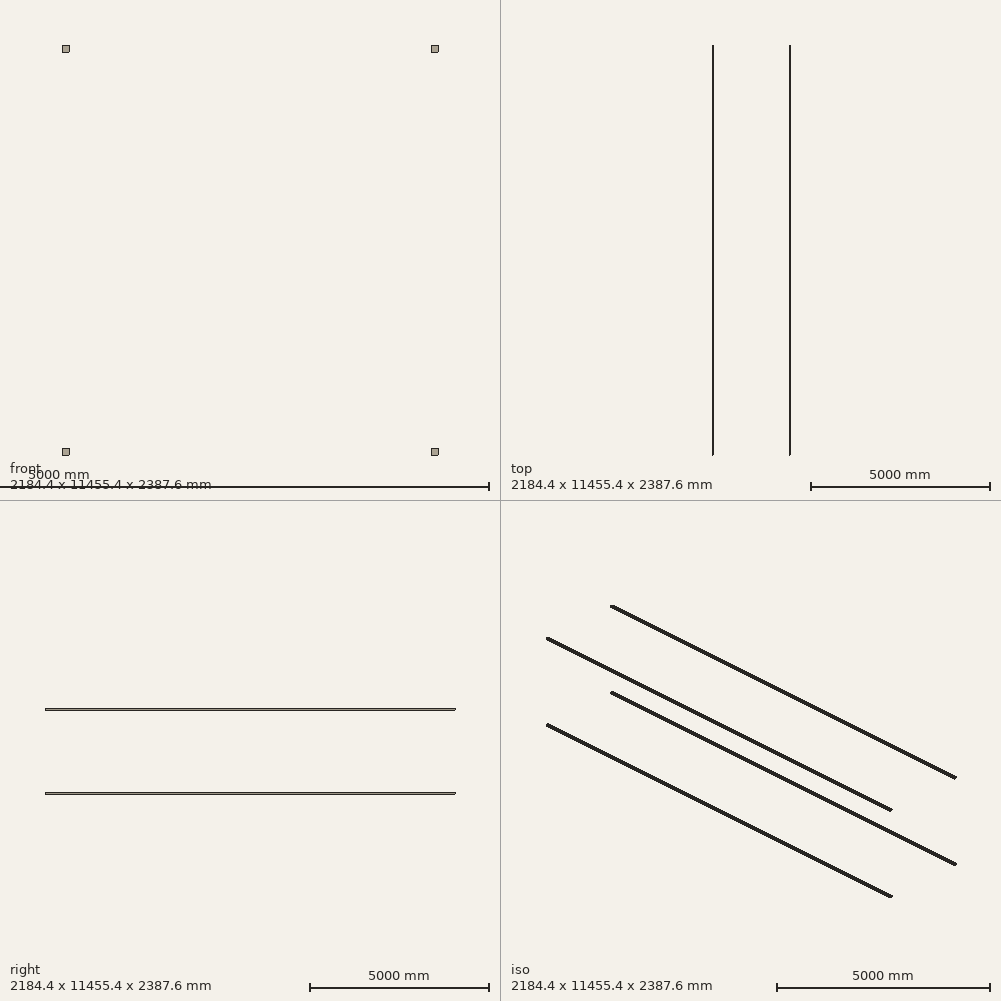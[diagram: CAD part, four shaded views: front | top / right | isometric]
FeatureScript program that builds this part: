
annotation { "Feature Type Name" : "Feature", "Feature Type Description" : "" }
export const myFeature = defineFeature(function(context is Context, id is Id, definition is map)
    precondition{}
    {
        {
            var Q0;
            Q0=qCreatedBy(makeId("Front.planeOp"),FACE);
            var sketch = newSketch(context, id + "F0", { "sketchPlane" : qUnion([Q0])});
            skLineSegment(sketch, "E0.bottom", {"start": v(-263.25, -179.2) * mm, "end": v(-225.15, -179.2) * mm});
            skLineSegment(sketch, "E0.top", {"start": v(-263.25, -217.3) * mm, "end": v(-225.15, -217.3) * mm});
            skLineSegment(sketch, "E0.left", {"start": v(-263.25, -179.2) * mm, "end": v(-263.25, -217.3) * mm});
            skLineSegment(sketch, "E0.right", {"start": v(-225.15, -179.2) * mm, "end": v(-225.15, -217.3) * mm});
            skLineSegment(sketch, "E1.bottom", {"start": v(1883.05, -179.2) * mm, "end": v(1921.15, -179.2) * mm});
            skLineSegment(sketch, "E1.top", {"start": v(1883.05, -217.3) * mm, "end": v(1921.15, -217.3) * mm});
            skLineSegment(sketch, "E1.left", {"start": v(1883.05, -179.2) * mm, "end": v(1883.05, -217.3) * mm});
            skLineSegment(sketch, "E1.right", {"start": v(1921.15, -179.2) * mm, "end": v(1921.15, -217.3) * mm});
            skLineSegment(sketch, "E2.bottom", {"start": v(1883.05, 2170.3) * mm, "end": v(1921.15, 2170.3) * mm});
            skLineSegment(sketch, "E2.top", {"start": v(1883.05, 2132.2) * mm, "end": v(1921.15, 2132.2) * mm});
            skLineSegment(sketch, "E2.left", {"start": v(1883.05, 2170.3) * mm, "end": v(1883.05, 2132.2) * mm});
            skLineSegment(sketch, "E2.right", {"start": v(1921.15, 2170.3) * mm, "end": v(1921.15, 2132.2) * mm});
            skLineSegment(sketch, "E3.bottom", {"start": v(-263.25, 2170.3) * mm, "end": v(-225.15, 2170.3) * mm});
            skLineSegment(sketch, "E3.top", {"start": v(-263.25, 2132.2) * mm, "end": v(-225.15, 2132.2) * mm});
            skLineSegment(sketch, "E3.left", {"start": v(-263.25, 2170.3) * mm, "end": v(-263.25, 2132.2) * mm});
            skLineSegment(sketch, "E3.right", {"start": v(-225.15, 2170.3) * mm, "end": v(-225.15, 2132.2) * mm});
            skSolve(sketch);
        }
        {
            var Q0;
            Q0=makeQuery(id+"F0.imprint","IMPRINT",FACE,{"disambiguationData":[TD([[makeQuery(id+"F0.imprint","IMPRINT",EDGE,{"derivedFrom":sQuery(id+"F0.wireOp",EDGE,"E2.bottom")}),-1.0]])]});
            var Q1;
            Q1=makeQuery(id+"F0.imprint","IMPRINT",FACE,{"disambiguationData":[TD([[makeQuery(id+"F0.imprint","IMPRINT",EDGE,{"derivedFrom":sQuery(id+"F0.wireOp",EDGE,"E0.bottom")}),-1.0]])]});
            var Q2;
            Q2=makeQuery(id+"F0.imprint","IMPRINT",FACE,{"disambiguationData":[TD([[makeQuery(id+"F0.imprint","IMPRINT",EDGE,{"derivedFrom":sQuery(id+"F0.wireOp",EDGE,"E3.bottom")}),-1.0]])]});
            var Q3;
            Q3=makeQuery(id+"F0.imprint","IMPRINT",FACE,{"disambiguationData":[TD([[makeQuery(id+"F0.imprint","IMPRINT",EDGE,{"derivedFrom":sQuery(id+"F0.wireOp",EDGE,"E1.bottom")}),-1.0]])]});
            extrude(context, id + "F1", {"entities" : qUnion([Q0, Q1, Q2, Q3]), "depth" : 11455.4 * mm, "offsetDistance" : 25.4 * mm});
        }
    });
